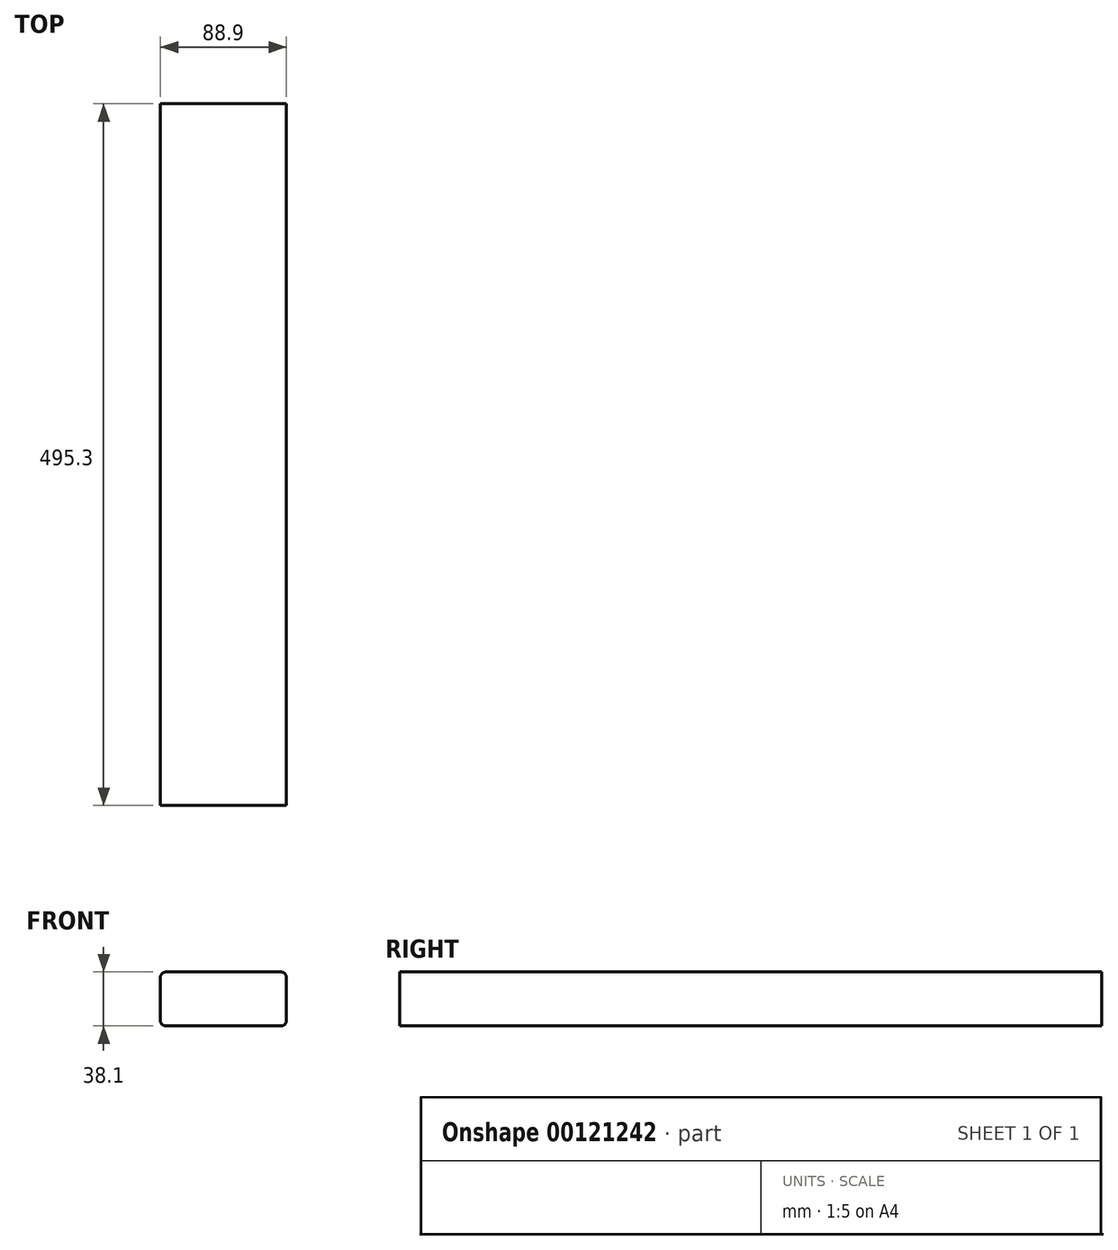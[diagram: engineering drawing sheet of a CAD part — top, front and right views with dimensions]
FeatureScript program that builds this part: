
annotation { "Feature Type Name" : "Feature", "Feature Type Description" : "" }
export const myFeature = defineFeature(function(context is Context, id is Id, definition is map)
    precondition{}
    {
        {
            var Q0;
            Q0=qCreatedBy(makeId("Front.planeOp"),FACE);
            var sketch = newSketch(context, id + "F0", { "sketchPlane" : qUnion([Q0])});
            skLineSegment(sketch, "E0.bottom", {"start": v(3.8, 0) * mm, "end": v(85.1, 0) * mm});
            skLineSegment(sketch, "E0.top", {"start": v(3.8, 38.1) * mm, "end": v(85.1, 38.1) * mm});
            skLineSegment(sketch, "E0.left", {"start": v(0, 3.81) * mm, "end": v(0, 34.3) * mm});
            skLineSegment(sketch, "E0.right", {"start": v(88.9, 3.81) * mm, "end": v(88.9, 34.29) * mm});
            skPoint(sketch, "E1.visualSharp", {"position": v(0, 38.1) * mm});
            skArc(sketch, "E1.filletArc", {"start": v(3.8, 38.1) * mm, "mid": v(1.12, 36.98) * mm, "end": v(0, 34.3) * mm});
            skPoint(sketch, "E2.visualSharp", {"position": v(0, 0) * mm});
            skArc(sketch, "E2.filletArc", {"start": v(0, 3.8) * mm, "mid": v(1.12, 1.12) * mm, "end": v(3.8, 0) * mm});
            skPoint(sketch, "E3.visualSharp", {"position": v(88.9, 0) * mm});
            skArc(sketch, "E3.filletArc", {"start": v(85.1, 0) * mm, "mid": v(87.78, 1.12) * mm, "end": v(88.9, 3.81) * mm});
            skPoint(sketch, "E4.visualSharp", {"position": v(88.9, 38.1) * mm});
            skArc(sketch, "E4.filletArc", {"start": v(88.9, 34.29) * mm, "mid": v(87.78, 36.98) * mm, "end": v(85.1, 38.1) * mm});
            skSolve(sketch);
        }
        {
            var Q0;
            Q0 = qSketchRegion(id + "F0", true);
            extrude(context, id + "F1", {"entities" : qUnion([Q0]), "depth" : 495.3 * mm});
        }
    });
